FCSTD DOCUMENT  (FreeCAD 0.16R6712 (Git))
Label: 20180220234525!LT_master_cad
License: All rights reserved
LicenseURL: http://en.wikipedia.org/wiki/All_rights_reserved
objects: Part::Feature×46, App::FeaturePython×30, Part::FeaturePython×23, App::DocumentObjectGroup×11, Sketcher::SketchObject×10, Part::Box×9, PartDesign::Pad×6, Part::Cylinder×5, Part::Compound×4, Part::MultiFuse×4, PartDesign::Pocket×2, Part::Cut×1, Part::Mirroring×1
note: 119 computed .brp shape members not serialized (recipe doc carries the construction recipe); baked Part::Feature solids carry a one-line shape summary decoded from their .brp

FEATURE [Part::Feature] Clone007  label="Cab - bottom right"
  Placement = pos=(-85.7284,2481.18,-691.277) rot=(0.57735,-0.57735,0.57735;4.18879rad)
  shape: bbox 1016 x 101.6 x 101.6 mm, 46 faces (baked)
FEATURE [Part::Feature] Clone012  label="Cab - bottom left"
  Placement = pos=(-84.0606,1566.05,-690.228) rot=(0.57735,-0.57735,0.57735;4.18879rad)
  shape: bbox 1016 x 101.6 x 101.6 mm, 46 faces (baked)
FEATURE [Part::Feature] Clone021  label="Cab - bottom rear"
  Placement = pos=(-34.9284,1617.58,-691.277) rot=(-1,0,0;1.5708rad)
  shape: bbox 101.6 x 812.8 x 101.6 mm, 38 faces (baked)
FEATURE [Part::Feature] Clone022  label="Cab - bottom front"
  Placement = pos=(879.472,1620.02,-691.277) rot=(-1,0,0;1.5708rad)
  shape: bbox 101.6 x 812.8 x 101.6 mm, 38 faces (baked)
FEATURE [Part::Box] Box002  label="Cab Vert 1"
  Height = 1422.4
  Length = 101.6
  Placement = pos=(830.339,1515.25,-639.428) rot=(0,0,1;0rad)
  Width = 101.6
FEATURE [Part::Feature] Box003  label="Cab Vert 2"
  Placement = pos=(-84.0606,1515.25,-639.428) rot=(0,0,1;0rad)
  shape: bbox 101.6 x 101.6 x 1321 mm, 6 faces (baked)
FEATURE [Part::Feature] Box004  label="Cab Vert 3"
  Placement = pos=(828.672,2430.38,-640.477) rot=(0,0,1;0rad)
  shape: bbox 101.6 x 101.6 x 1321 mm, 6 faces (baked)
FEATURE [Part::Feature] Box005  label="Cab Vert 4"
  Placement = pos=(-86.1858,2430.38,-640.477) rot=(0,0,1;0rad)
  shape: bbox 101.6 x 101.6 x 1321 mm, 6 faces (baked)
FEATURE [Part::Feature] Clone023  label="Cab - bottom right001"
  Placement = pos=(-92.3505,2481.18,731.123) rot=(0.57735,-0.57735,0.57735;4.18879rad)
  shape: bbox 1016 x 101.6 x 101.6 mm, 46 faces (baked)
FEATURE [Part::Feature] Clone024  label="Cab - bottom front001"
  Placement = pos=(872.85,1620.02,731.123) rot=(-1,0,0;1.5708rad)
  shape: bbox 101.6 x 812.8 x 101.6 mm, 38 faces (baked)
FEATURE [Part::Feature] Clone025  label="Cab - bottom left001"
  Placement = pos=(-90.6827,1566.05,732.172) rot=(0.57735,-0.57735,0.57735;4.18879rad)
  shape: bbox 1016 x 101.6 x 101.6 mm, 46 faces (baked)
FEATURE [Part::Feature] Clone026  label="Cab - bottom rear001"
  Placement = pos=(-41.5505,1617.58,731.123) rot=(-1,0,0;1.5708rad)
  shape: bbox 101.6 x 812.8 x 101.6 mm, 38 faces (baked)
FEATURE [Part::Cylinder] Cylinder014  label="Person"
  Angle = 360
  Height = 1524
  Placement = pos=(-1660.29,1661.1,-1132.53) rot=(0,0,1;0rad)
  Radius = 254
FEATURE [Part::Box] Box006  label="Cab Top"
  Height = 3.175
  Length = 1016
  Placement = pos=(-92.3505,1516.16,787.4) rot=(0,0,1;0rad)
  Width = 1016
FEATURE [Part::Box] Box007  label="Cab Side"
  Height = 1524
  Length = 1016
  Placement = pos=(-84.8788,1511.3,-739.16) rot=(0,0,1;0rad)
  Width = 3.175
FEATURE [Part::Feature] Box008  label="Cab Side001"
  Placement = pos=(-93.1687,2532.38,-739.16) rot=(0,0,1;0rad)
  shape: bbox 1016 x 3.175 x 1524 mm, 6 faces (baked)
FEATURE [Part::Feature] Box009  label="Cab Side002"
  Placement = pos=(-93.98,2529.04,-739.16) rot=(0,0,-1;1.5708rad)
  shape: bbox 3.175 x 1016 x 1524 mm, 6 faces (baked)
FEATURE [Part::Feature] Box010  label="Cab Side003"
  Placement = pos=(-88.1961,2529.04,-739.16) rot=(0,0,-1;1.5708rad)
  shape: bbox 3.175 x 1016 x 1524 mm, 6 faces (baked)
FEATURE [Part::Box] Box011  label="Cab Bottom"
  Height = 3.175
  Length = 1016
  Placement = pos=(-92.3505,1516.16,-746.76) rot=(0,0,1;0rad)
  Width = 1016
FEATURE [App::DocumentObjectGroup] Group  label="Cab"
  Group = -> [Box005,Box004,Box003,Box002,Clone007,Clone012,Clone021,Clone022,Box006,Box007,Box008,Box009,Box010,Box011,Clone023,Clone024,Clone025,Clone026]
FEATURE [Part::Feature] Clone034  label="Frame - horizontal R"
  Placement = pos=(-1253.88,1464.81,-791.981) rot=(0,1,0;1.5708rad)
  shape: bbox 2134 x 101.6 x 101.6 mm, 90 faces (baked)
FEATURE [Part::Feature] Box  label="PowerCube005"
  Placement = pos=(-1231.18,2023.04,-741.072) rot=(0,0,1;0rad)
  shape: bbox 762 x 508 x 508 mm, 6 faces (baked)
FEATURE [Part::Feature] Box014  label="PowerCube006"
  Placement = pos=(-1228.85,1515.61,-739.279) rot=(0,0,1;0rad)
  shape: bbox 762 x 508 x 508 mm, 6 faces (baked)
FEATURE [Part::Feature] Compound022  label="Idler007"
  Placement = pos=(464.548,1400.81,-1066.8) rot=(0,0,1;0rad)
  shape: bbox 302.3 x 217 x 302.3 mm, 148 faces, 13 solids (baked)
FEATURE [Part::Feature] Compound  label="Idler008"
  Placement = pos=(-948.365,1400.81,-1066.8) rot=(0,0,1;0rad)
  shape: bbox 302.3 x 217 x 302.3 mm, 148 faces, 13 solids (baked)
FEATURE [Part::Feature] Compound025  label="Idler011"
  Placement = pos=(464.566,2966.33,-1066.8) rot=(0,0,1;0rad)
  shape: bbox 302.3 x 217 x 302.3 mm, 148 faces, 13 solids (baked)
FEATURE [Part::FeaturePython] PathArray002  # WARN: FeaturePython — macro-defined, semantics opaque (R4)
  Align = true
  Count = 52
  Placement = pos=(0,1235.71,0) rot=(0,0,1;0rad)
  Xlate = (0,0,0)
FEATURE [Part::FeaturePython] PathArray003  # WARN: FeaturePython — macro-defined, semantics opaque (R4)
  Align = true
  Count = 52
  Placement = pos=(0,2810.51,0) rot=(0,0,1;0rad)
  Xlate = (0,0,0)
FEATURE [Part::Cylinder] Cylinder
  Angle = 360
  Height = 1828.8
  Placement = pos=(-892.81,1108.71,-914.4) rot=(0.57735,-0.57735,-0.57735;4.18879rad)
  Radius = 38.1
FEATURE [Part::Cylinder] Cylinder018
  Angle = 360
  Height = 1828.8
  Placement = pos=(520.7,1108.71,-914.4) rot=(0.57735,-0.57735,-0.57735;4.18879rad)
  Radius = 38.1
FEATURE [Part::Feature] Compound026  label="Idler012"
  Placement = pos=(-947.42,2966.33,-1066.8) rot=(0,0,1;0rad)
  shape: bbox 302.3 x 217 x 302.3 mm, 148 faces, 13 solids (baked)
FEATURE [Part::Feature] Cylinder035
  Placement = pos=(1556.05,1344.57,-44.0571) rot=(-0.577258,0.577258,-0.577534;2.09412rad)
  shape: bbox 812.8 x 76.2 x 76.59 mm, 3 faces (baked)
FEATURE [Part::Feature] Cylinder036
  Placement = pos=(2058.87,1344.57,-43.8629) rot=(-0.577258,0.577258,-0.577534;2.09412rad)
  shape: bbox 508 x 35.56 x 35.8 mm, 3 faces (baked)
FEATURE [Part::Feature] Cylinder037
  Placement = pos=(2551.89,1307.89,-43.6273) rot=(-1,-0.000239,-0.000239;1.5708rad)
  shape: bbox 50.8 x 76.2 x 50.8 mm, 3 faces (baked)
FEATURE [Part::Feature] Cylinder038
  Placement = pos=(1377.14,1307.13,-44.0667) rot=(-1,-0.000239,-0.000239;1.5708rad)
  shape: bbox 50.8 x 76.2 x 50.8 mm, 3 faces (baked)
FEATURE [Part::Feature] Compound031  label="Idler013"
  Placement = pos=(-210.82,2966.21,-1066.8) rot=(0,0,1;0rad)
  shape: bbox 302.3 x 217 x 302.3 mm, 148 faces, 13 solids (baked)
FEATURE [Part::Feature] Compound033  label="Idler015"
  Placement = pos=(-210.82,1391.41,-1066.8) rot=(0,0,1;0rad)
  shape: bbox 302.3 x 217 x 302.3 mm, 148 faces, 13 solids (baked)
FEATURE [Part::Cylinder] Cylinder043
  Angle = 360
  Height = 1828.8
  Placement = pos=(-156.21,1108.71,-914.4) rot=(0.57735,-0.57735,-0.57735;4.18879rad)
  Radius = 38.1
FEATURE [App::DocumentObjectGroup] Group004  label="Idlers"
  Group = -> [Cylinder018,Cylinder,Compound026,Compound025,Compound,Compound022,Cylinder043,Compound031,Compound033]
FEATURE [Part::Feature] Box015  label="PowerCube007"
  Placement = pos=(-1180.34,2023.04,-233.172) rot=(0,0,1;0rad)
  shape: bbox 762 x 508 x 508 mm, 6 faces (baked)
FEATURE [Part::Feature] Box016  label="PowerCube008"
  Placement = pos=(-1180.34,1515.11,-233.172) rot=(0,0,1;0rad)
  shape: bbox 762 x 508 x 508 mm, 6 faces (baked)
FEATURE [Part::Box] Box017  label="Cube"
  Height = 1524
  Length = 1041.4
  Placement = pos=(-266.7,1567.18,-736.6) rot=(0,0,1;0rad)
  Width = 914.4
FEATURE [Part::Feature] Clone063001  label="LT_arm_shaft"
  Placement = pos=(-1028.09,1261.61,54.5351) rot=(0.57735,-0.57735,-0.57735;4.18879rad)
  shape: bbox 76.2 x 1524 x 76.2 mm, 3 faces (baked)
FEATURE [Sketcher::SketchObject] Sketch
  ExternalGeometry = -> [Cylinder035]
  Placement = pos=(1556.05,1344.57,-44.0571) rot=(-0.577442,0.577442,0.577166;4.18851rad)
  Support = -> Cylinder035 [Face3]
  sketch-geometry (1):
    g0: Circle CenterX=5e-12 CenterY=0 CenterZ=0 NormalX=0 NormalY=0 NormalZ=1 Radius=38.1
  constraints (2):
    c: Coincident(g0,g-3)
    c: Tangent(g0,g-3)
FEATURE [PartDesign::Pad] Pad008
  Length = 152.4
  Length2 = 100
  Placement = pos=(1556.05,1344.57,-44.0571) rot=(-0.577258,0.577258,-0.577534;2.09412rad)
  Sketch = -> Sketch
  Type = 0
FEATURE [Part::Feature] Cylinder044
  Placement = pos=(3466.29,1307.89,-196.027) rot=(-1,-0.000239,-0.000239;1.5708rad)
  shape: bbox 50.8 x 76.2 x 50.8 mm, 3 faces (baked)
FEATURE [Part::Feature] Cylinder045
  Placement = pos=(2724.36,1344.57,-196.263) rot=(-0.577258,0.577258,-0.577534;2.09412rad)
  shape: bbox 508 x 35.56 x 35.8 mm, 3 faces (baked)
FEATURE [Part::Feature] Cylinder046
  Placement = pos=(1377.14,1307.13,-196.467) rot=(-1,-0.000239,-0.000239;1.5708rad)
  shape: bbox 50.8 x 76.2 x 50.8 mm, 3 faces (baked)
FEATURE [Sketcher::SketchObject] Sketch016
  ExternalGeometry = -> [Cylinder045]
  Placement = pos=(2724.36,1344.57,-196.263) rot=(-0.577442,0.577442,0.577166;4.18851rad)
  Support = -> Cylinder045 [Face3]
  sketch-geometry (1):
    g0: Circle CenterX=0 CenterY=0 CenterZ=0 NormalX=0 NormalY=0 NormalZ=1 Radius=17.78
  constraints (2):
    c: Coincident(g0,g-1)
    c: Tangent(g0,g-3)
FEATURE [PartDesign::Pad] Pad008003
  Length = 609.6
  Length2 = 100
  Placement = pos=(2724.36,1344.57,-196.263) rot=(-0.577258,0.577258,-0.577534;2.09412rad)
  Sketch = -> Sketch016
  Type = 0
FEATURE [Part::FeaturePython] Arm_support_01  # a2plus imported part (geometry in sourceFile) (typed FeaturePython)
  Placement = pos=(-359.342,1668.01,-741.182) rot=(0,0,1;0rad)
  fixedPosition = true
  sourceFile = <userpath>/Documents/Freecad docs/Tractor/LT/Arm support.fcstd
  timeLastImport = 1.50929e+09
  updateColors = true
FEATURE [Part::Feature] Arm_support_01003  label="Arm_support_004"
  Placement = pos=(-359.342,2379.21,-741.182) rot=(0,0,1;0rad)
  shape: bbox 101.6 x 101.6 x 1016 mm, 46 faces (baked)
FEATURE [Part::Feature] Arm_support_01004  label="10 hole tubing front"
  Placement = pos=(727.318,2531.61,-791.982) rot=(1,0,0;1.5708rad)
  shape: bbox 101.6 x 1016 x 101.6 mm, 46 faces (baked)
FEATURE [App::FeaturePython] planeConstraint01  label="10 hole tubing front 1"  # a2plus constraint (typed FeaturePython)
  Object1 = Arm_support_01004
  Object2 = Arm_support_01
  SubElement1 = Face4
  SubElement2 = Face1
  Type = plane
  directionConstraint = 1
  offset = 203.2
FEATURE [App::FeaturePython] planeConstraint01_mirror  label="planeConstraint01__Arm_support_005"  # a2plus constraint (typed FeaturePython)
  Object1 = Arm_support_01004
  Object2 = Arm_support_01
  SubElement1 = Face4
  SubElement2 = Face1
  Type = plane
  directionConstraint = 1
  offset = 203.2
FEATURE [App::FeaturePython] planeConstraint02  label="10 hole tubing front 2"  # a2plus constraint (typed FeaturePython)
  Object1 = Arm_support_01004
  Object2 = Arm_support_01
  SubElement1 = Face1
  SubElement2 = Face3
  Type = plane
  directionConstraint = 0
  offset = 0
FEATURE [App::FeaturePython] planeConstraint02_mirror  label="planeConstraint02__Arm_support_005"  # a2plus constraint (typed FeaturePython)
  Object1 = Arm_support_01004
  Object2 = Arm_support_01
  SubElement1 = Face1
  SubElement2 = Face3
  Type = plane
  directionConstraint = 0
  offset = 0
FEATURE [App::FeaturePython] planeConstraint03  label="planeConstraint03__Arm_support_005"  # a2plus constraint (typed FeaturePython)
  Object1 = Arm_support_01
  Object2 = Arm_support_01004
  SubElement1 = Face5
  SubElement2 = Face5
  Type = plane
  directionConstraint = 0
  offset = -1086.66
FEATURE [App::FeaturePython] planeConstraint03_mirror  label="10 hole tubing front 3"  # a2plus constraint (typed FeaturePython)
  Object1 = Arm_support_01
  Object2 = Arm_support_01004
  SubElement1 = Face5
  SubElement2 = Face5
  Type = plane
  directionConstraint = 0
  offset = -1086.66
FEATURE [Part::Feature] Arm_support_01005  label="10 hole tubing rear"
  Placement = pos=(-1203.08,2531.61,-791.982) rot=(1,0,0;1.5708rad)
  shape: bbox 101.6 x 1016 x 101.6 mm, 46 faces (baked)
FEATURE [Part::Feature] Arm_support_01006  label="10 hole tubing mid 1"
  Placement = pos=(-720.479,2531.61,-791.982) rot=(1,0,0;1.5708rad)
  shape: bbox 101.6 x 1016 x 101.6 mm, 46 faces (baked)
FEATURE [Part::Feature] Pad008003002  label="Pad008005"
  Placement = pos=(-1.27,0,0) rot=(0,0,1;0rad)
  shape: bbox 965.2 x 76.2 x 76.66 mm, 3 faces (baked)
FEATURE [Part::Feature] Pad008003003  label="Pad008006"
  Placement = pos=(-1.27,0,-152.4) rot=(0,0,1;0rad)
  shape: bbox 965.2 x 76.2 x 76.66 mm, 3 faces (baked)
FEATURE [Part::Feature] Pad008003004  label="Pad008007"
  Placement = pos=(242.56,0,0) rot=(0,0,1;0rad)
  shape: bbox 1118 x 35.56 x 36.09 mm, 3 faces (baked)
FEATURE [Part::Compound] Compound001004
  Links = -> [Pad008003002,Cylinder036,Cylinder037,Cylinder038]
FEATURE [Part::Compound] Compound001005
  Links = -> [Pad008003004,Cylinder046,Cylinder044,Pad008003003]
FEATURE [App::DocumentObjectGroup] Group009  label="Cylinders (edit here)"
  Group = -> [Cylinder035,Pad008,Cylinder045,Pad008003,Compound001004,Compound001005]
FEATURE [Part::Box] Box020  label="Cube001"
  Height = 508
  Length = 508
  Placement = pos=(-943.542,1515.61,-741.182) rot=(0,0,1;0rad)
  Width = 330.2
FEATURE [Part::Box] Box021  label="Cube002"
  Height = 508
  Length = 508
  Placement = pos=(-943.542,2201.41,-741.182) rot=(0,0,1;0rad)
  Width = 330.2
FEATURE [Part::Box] Box022  label="Cube003"
  Height = 508
  Length = 508
  Placement = pos=(-943.542,1769.61,-741.182) rot=(0,0,1;1.5708rad)
  Width = 330.2
FEATURE [Part::Box] Box023  label="Cube004"
  Height = 508
  Length = 508
  Placement = pos=(-918.14,1642.61,-233.182) rot=(0,0,1;0rad)
  Width = 762
FEATURE [App::DocumentObjectGroup] Group013  label="Small PC"
  Group = -> [Box020,Box021,Box022,Box023]
FEATURE [App::DocumentObjectGroup] Group002  label="Power Cube"
  Group = -> [Box,Box014,Box015,Box016,Group013]
FEATURE [Part::Feature] Arm_support_01006001  label="10 hole tubing mid 2"
  Placement = pos=(-359.342,2531.61,-791.982) rot=(1,0,0;1.5708rad)
  shape: bbox 101.6 x 1016 x 101.6 mm, 46 faces (baked)
FEATURE [App::FeaturePython] planeConstraint26  label="10 hole mid 2"  # a2plus constraint (typed FeaturePython)
  Object1 = Arm_support_01006001
  Object2 = Arm_support_01
  SubElement1 = Face5
  SubElement2 = Face5
  Type = plane
  directionConstraint = 0
  offset = 0
FEATURE [App::FeaturePython] planeConstraint26_mirror  label="planeConstraint26__10 hole tubing mid 2"  # a2plus constraint (typed FeaturePython)
  Object1 = Arm_support_01006001
  Object2 = Arm_support_01
  SubElement1 = Face5
  SubElement2 = Face5
  Type = plane
  directionConstraint = 0
  offset = 0
FEATURE [App::FeaturePython] planeConstraint27_mirror001  label="planeConstraint27__Arm_support_004"  # a2plus constraint (typed FeaturePython)
  Object1 = Arm_support_01003
  Object2 = Arm_support_01
  SubElement1 = Face16
  SubElement2 = Face16
  Type = plane
  directionConstraint = 0
  offset = -711.2
FEATURE [Part::Feature] Compound001001  label="Track tensioner"
  Placement = pos=(105.497,-20.1003,38.1) rot=(0,0,1;0rad)
  shape: bbox 248.4 x 1599 x 248.4 mm, 472 faces, 10 solids (baked)
FEATURE [App::DocumentObjectGroup] Group005  label="Tracks"
  Group = -> [PathArray002,PathArray003,Compound001001]
FEATURE [App::FeaturePython] planeConstraint28  label="tensioner 1"  # a2plus constraint (typed FeaturePython)
  Object1 = Compound001001
  Object2 = Arm_support_01
  SubElement1 = Face52
  SubElement2 = Face1
  Type = plane
  directionConstraint = 1
  offset = -1.27
FEATURE [App::FeaturePython] planeConstraint28_mirror  label="planeConstraint28__Compound002"  # a2plus constraint (typed FeaturePython)
  Object1 = Compound001001
  Object2 = Arm_support_01
  SubElement1 = Face52
  SubElement2 = Face1
  Type = plane
  directionConstraint = 1
  offset = -1.27
FEATURE [App::FeaturePython] planeConstraint29  label="planeConstraint29__Compound002"  # a2plus constraint (typed FeaturePython)
  Object1 = Arm_support_01
  Object2 = Compound001001
  SubElement1 = Face5
  SubElement2 = Face51
  Type = plane
  directionConstraint = 1
  offset = -1.27
FEATURE [App::FeaturePython] planeConstraint29_mirror  label="tensioner 2"  # a2plus constraint (typed FeaturePython)
  Object1 = Arm_support_01
  Object2 = Compound001001
  SubElement1 = Face5
  SubElement2 = Face51
  Type = plane
  directionConstraint = 1
  offset = -1.27
FEATURE [App::DocumentObjectGroup] Group011  label="Constraints (permanent)"
  Group = -> [Arm_support_01,planeConstraint01,planeConstraint02,planeConstraint03_mirror,planeConstraint26,planeConstraint28,planeConstraint29_mirror]
FEATURE [Part::FeaturePython] Clone063026  label="8 hole tubing"  # WARN: FeaturePython — macro-defined, semantics opaque (R4)
  Placement = pos=(-1213.84,1566.41,-754.372) rot=(0,1,0;0.202167rad)
  Scale = (1,1,1)
FEATURE [Part::FeaturePython] Clone063027  label="8 hole tubing001"  # WARN: FeaturePython — macro-defined, semantics opaque (R4)
  Placement = pos=(-1106.73,2480.81,22.8013) rot=(0,1,0;1.32645rad)
  Scale = (1,1,1)
FEATURE [Part::FeaturePython] Clone063028  label="8 hole tubing002"  # WARN: FeaturePython — macro-defined, semantics opaque (R4)
  Placement = pos=(-1213.84,2480.81,-754.372) rot=(0,1,0;0.202167rad)
  Scale = (1,1,1)
FEATURE [Part::FeaturePython] Clone063029  label="8 hole tubing003"  # WARN: FeaturePython — macro-defined, semantics opaque (R4)
  Placement = pos=(-1106.73,1566.41,22.8013) rot=(0,1,0;1.32645rad)
  Scale = (1,1,1)
FEATURE [Part::FeaturePython] Clone063033  label="Cylinder 36in retracted"  # Draft clone (typed FeaturePython)
  Objects = -> [Compound001004]
  Placement = pos=(-1736.48,119.579,-239.915) rot=(0,0,1;0rad)
  Scale = (1,1,1)
FEATURE [Part::FeaturePython] Clone063034  label="Cylinder 36in extended"  # Draft clone (typed FeaturePython)
  Objects = -> [Compound001005]
  Placement = pos=(-557.972,119.579,-1660.81) rot=(0,-1,0;1.56923rad)
  Scale = (1,1,1)
FEATURE [Sketcher::SketchObject] Sketch024  label="Arm-Cylinder geometry"
  Placement = pos=(-15.2649,852.156,-47.0649) rot=(1,0,0;1.5708rad)
  sketch-geometry (38):
    g0: LineSegment StartX=1203.73 StartY=-906.649 StartZ=0 EndX=1301 EndY=-728.242 EndZ=0
    g1: LineSegment StartX=1301 StartY=-728.242 StartZ=0 EndX=2088.08 EndY=-1092.2 EndZ=0
    g2: LineSegment StartX=601.383 StartY=-1092.2 StartZ=0 EndX=1685.52 EndY=-1092.2 EndZ=0
    g3: LineSegment StartX=-1012.82 StartY=101.6 StartZ=0 EndX=1203.73 EndY=-906.649 EndZ=0
    g4: Circle [constr] CenterX=-1012.82 CenterY=101.6 CenterZ=0 NormalX=0 NormalY=0 NormalZ=1 Radius=2435.1
    g5: LineSegment StartX=565.984 StartY=2188.85 StartZ=0 EndX=1016.32 EndY=1447.8 EndZ=0
    g6: LineSegment StartX=385.75 StartY=2095.01 StartZ=0 EndX=565.984 EndY=2188.85 EndZ=0
    g7: LineSegment StartX=-1012.82 StartY=101.6 StartZ=0 EndX=385.75 EndY=2095.01 EndZ=0
    g8: LineSegment StartX=-252.055 StartY=-693.674 StartZ=0 EndX=789.345 EndY=-693.674 EndZ=0
    g9: LineSegment StartX=789.345 StartY=-693.674 StartZ=0 EndX=789.345 EndY=830.326 EndZ=0
    g10: LineSegment StartX=789.345 StartY=830.326 StartZ=0 EndX=-252.055 EndY=830.326 EndZ=0
    g11: LineSegment StartX=-252.055 StartY=830.326 StartZ=0 EndX=-252.055 EndY=-693.674 EndZ=0
    g12: LineSegment StartX=-1012.82 StartY=101.6 StartZ=0 EndX=904.459 EndY=-143.324 EndZ=0
    g13: LineSegment StartX=904.459 StartY=-143.324 StartZ=0 EndX=1203.73 EndY=-906.649 EndZ=0
    g14: LineSegment StartX=-1012.82 StartY=101.6 StartZ=0 EndX=-419.585 EndY=1941.17 EndZ=0
    g15: LineSegment StartX=-419.585 StartY=1941.17 StartZ=0 EndX=385.75 EndY=2095.01 EndZ=0
    g16: LineSegment StartX=-395.479 StartY=2049.21 StartZ=0 EndX=-276.62 EndY=1968.48 EndZ=0
    g17: LineSegment StartX=-342.9 StartY=-236.474 StartZ=0 EndX=831.85 EndY=-236.474 EndZ=0
    g18: LineSegment StartX=-341.372 StartY=1852.68 StartZ=0 EndX=-342.9 EndY=-236.474 EndZ=0
    g19: LineSegment StartX=-1012.82 StartY=101.6 StartZ=0 EndX=-341.372 EndY=1852.68 EndZ=0
    g20: LineSegment StartX=-1012.82 StartY=101.6 StartZ=0 EndX=831.85 EndY=-236.474 EndZ=0
    g21: LineSegment StartX=1015.09 StartY=-147.156 StartZ=0 EndX=957.587 EndY=-278.831 EndZ=0
    g22: LineSegment StartX=1015.09 StartY=-147.156 StartZ=0 EndX=1203.73 EndY=-906.649 EndZ=0
    g23: LineSegment StartX=-395.479 StartY=2049.21 StartZ=0 EndX=385.75 EndY=2095.01 EndZ=0
    g24: LineSegment StartX=1015.09 StartY=-147.156 StartZ=0 EndX=883.415 EndY=-89.6516 EndZ=0
    g25: LineSegment StartX=-395.479 StartY=2049.21 StartZ=0 EndX=-476.211 EndY=1930.35 EndZ=0
    g26: LineSegment StartX=-395.479 StartY=2049.21 StartZ=0 EndX=214.076 EndY=2137.74 EndZ=0
    g27: LineSegment StartX=214.076 StartY=2137.74 StartZ=0 EndX=565.984 EndY=2188.85 EndZ=0
    g28: LineSegment StartX=1301 StartY=-728.242 StartZ=0 EndX=1029.07 EndY=-175.57 EndZ=0
    g29: LineSegment StartX=1015.09 StartY=-147.156 StartZ=0 EndX=1029.07 EndY=-175.57 EndZ=0
    g30: LineSegment StartX=963.525 StartY=-293.978 StartZ=0 EndX=831.85 EndY=-236.474 EndZ=0
    g31: LineSegment StartX=831.85 StartY=-236.474 StartZ=0 EndX=889.354 EndY=-104.799 EndZ=0
    g32: LineSegment StartX=-260.64 StartY=1971.53 StartZ=0 EndX=-341.372 EndY=1852.68 EndZ=0
    g33: LineSegment StartX=-341.372 StartY=1852.68 StartZ=0 EndX=-460.231 EndY=1933.41 EndZ=0
    g34: LineSegment StartX=1203.73 StartY=-906.649 StartZ=0 EndX=1353.99 EndY=-1092.2 EndZ=0
    g35: LineSegment StartX=1353.99 StartY=-1092.2 StartZ=0 EndX=2088.08 EndY=-1092.2 EndZ=0
    g36: LineSegment StartX=406.99 StartY=1857.2 StartZ=0 EndX=1016.32 EndY=1447.8 EndZ=0
    g37: LineSegment StartX=385.75 StartY=2095.01 StartZ=0 EndX=406.99 EndY=1857.2 EndZ=0
  constraints (106):
    c: Coincident(g1,g0)
    c: Horizontal(g2)
    c: Coincident(g3,g0)
    c: DistanceX(g8) = -252.055
    c: Distance(g0) = 203.2
    c: Distance(g1) = 867.156
    c: PointOnObject(g0,g4)
    c: Coincident(g5,g6)
    c: Coincident(g7,g6)
    c: Equal(g3,g7) = 2071.24
    c: Equal(g0,g6) = 238.711
    c: Equal(g1,g5) = 1020.15
    c: Coincident(g8,g9)
    c: Coincident(g9,g10)
    c: Coincident(g10,g11)
    c: Coincident(g11,g8)
    c: Horizontal(g8)
    c: Horizontal(g10)
    c: Vertical(g9)
    c: Vertical(g11)
    c: Distance(g10) = 1041.4
    c: Distance(g9) = 1524
    c: Coincident(g12,g13)
    c: Coincident(g13,g0)
    c: Coincident(g14,g15)
    c: Equal(g12,g14) = 1727.2
    c: Equal(g13,g15) = 711.2
    c: DistanceY(g2) = -1092.2
    c: Distance(g5,g2) = 2540
    c: Distance(g18,g14) = 101.6
    c: PointOnObject(g16,g15)
    c: Distance(g16,g15) = 101.6
    c: Distance(g17) = 1174.75
    c: Coincident(g18,g17)
    c: Distance(g18) = 2089.15
    c: Equal(g19,g20)
    c: PointOnObject(g21,g13)
    c: Distance(g21,g13) = 101.6
    c: Coincident(g22,g0)
    c: Equal(g23,g22)
    c: DistanceY(g8) = -693.674
    c: Distance(g17,g8) = 457.2
    c: PointOnObject(g5,g4)
    c: Horizontal(g17)
    c: Coincident(g23,g16)
    c: Coincident(g22,g21)
    c: Coincident(g24,g21)
    c: PointOnObject(g24,g13)
    c: Perpendicular(g21,g24)
    c: Equal(g24,g21)
    c: Coincident(g25,g16)
    c: Equal(g25,g16)
    c: Perpendicular(g16,g25)
    c: PointOnObject(g25,g15)
    c: Coincident(g27,g5)
    c: Coincident(g26,g27)
    c: Coincident(g26,g16)
    c: Parallel(g27,g26)
    c: Distance(g27) = 355.6
    c: Coincident(g28,g0)
    c: Equal(g26,g28)
    c: Distance(g26) = 615.95
    c: Coincident(g29,g21)
    c: Coincident(g29,g28)
    c: Parallel(g29,g28)
    c: Coincident(g17,g20)
    c: Coincident(g17,g30)
    c: Coincident(g17,g31)
    c: Perpendicular(g30,g31)
    c: Equal(g31,g30)
    c: PointOnObject(g30,g13)
    c: PointOnObject(g31,g13)
    c: Distance(g17,g13) = 101.6
    c: Perpendicular(g32,g33)
    c: Equal(g33,g32)
    c: PointOnObject(g33,g15)
    c: Coincident(g32,g33)
    c: PointOnObject(g32,g15)
    c: Coincident(g32,g18)
    c: Coincident(g32,g19)
    c: Distance(g18,g15) = 101.6
    c: Coincident(g3,g4)
    c: Coincident(g3,g7)
    c: Coincident(g3,g12)
    c: Coincident(g3,g14)
    c: Coincident(g3,g19)
    c: Coincident(g3,g20)
    c: DistanceX(g17) = -342.9
    c: Coincident(g0,g34)
    c: Coincident(g34,g35)
    c: Coincident(g35,g1)
    c: Distance(g34) = 238.76
    c: Angle(g35,g34) = 2.25147
    c: Angle(g34,g0) = 1.96175
    c: Coincident(g37,g36)
    c: Equal(g34,g37) = 238.76
    c: Angle(g36,g37) = 2.25147
    c: Coincident(g15,g23)
    c: Coincident(g15,g6)
    c: Coincident(g6,g37)
    c: Coincident(g36,g5)
    c: Angle(g37,g6) = 1.96175
    c: DistanceY(g24) = -89.6516
    c: Horizontal(g35)
    c: PointOnObject(g1,g2)
    c: DistanceY(g-1,g3) = 101.6
FEATURE [Part::Cylinder] Cylinder047  label="Loader cylinder shaft"
  Angle = 360
  Height = 1219.2
  Placement = pos=(-359.342,1414.01,-283.982) rot=(-1,0,0;1.5708rad)
  Radius = 25.4
FEATURE [App::FeaturePython] planeConstraint30_mirror  label="planeConstraint30__Arm_support_01"  # a2plus constraint (typed FeaturePython)
  Object1 = Arm_support_01
  Object2 = Pocket002
  SubElement1 = Face16
  SubElement2 = Face1
  Type = plane
  directionConstraint = 1
  offset = 0
FEATURE [App::FeaturePython] axialConstraint04_mirror  label="axialConstraint04__Arm_support_01"  # a2plus constraint (typed FeaturePython)
  Object1 = Arm_support_01
  Object2 = Pocket002
  SubElement1 = Edge30
  SubElement2 = Edge15
  Type = axial
  directionConstraint = 1
  lockRotation = false
FEATURE [Part::Feature] Compound001  label="Lowered bucket"
  Placement = pos=(2340.99,3211.4,388.012) rot=(0,-1,0;0.240855rad)
  shape: bbox 1093 x 1829 x 510.4 mm, 626 faces, 28 solids (baked)
FEATURE [Part::Feature] Compound001009  label="Raised bucket"
  Placement = pos=(2138.11,3211.4,2098.75) rot=(0,1,0;0.5916rad)
  shape: bbox 788.7 x 1829 x 923.9 mm, 626 faces, 28 solids (baked)
FEATURE [Part::Feature] Fusion002002002  label="14" cylinder ret"
  Placement = pos=(-2279.03,188.997,-2348.22) rot=(0.62855,0.729863,-0.268748;1.8185rad)
  shape: bbox 298.4 x 50.8 x 614.8 mm, 38 faces (baked)
FEATURE [Part::Feature] Fusion002002001  label="14" cylinder ext"
  Placement = pos=(146.458,-4455.83,-1155.72) rot=(0.957629,0.161054,0.238764;1.1564rad)
  shape: bbox 1013 x 50.8 x 186 mm, 38 faces (baked)
FEATURE [App::FeaturePython] circularEdgeConstraint10  label="curl cylinder ret"  # a2plus constraint (typed FeaturePython)
  Object1 = Fusion002002002
  Object2 = Compound001
  SubElement1 = Edge79
  SubElement2 = Edge986
  Type = circularEdge
  directionConstraint = 1
  lockRotation = false
  offset = 0
FEATURE [App::FeaturePython] circularEdgeConstraint11  label="curl cylinder ext"  # a2plus constraint (typed FeaturePython)
  Object1 = Fusion002002001
  Object2 = Compound001009
  SubElement1 = Edge62
  SubElement2 = Edge986
  Type = circularEdge
  directionConstraint = 1
  lockRotation = false
  offset = 0
FEATURE [Sketcher::SketchObject] Sketch031
  Placement = pos=(879.717,1464.81,-791.981) rot=(0,1,0;1.5708rad)
  Support = -> Clone034 [Face4]
  sketch-geometry (4):
    g0: LineSegment StartX=-50.8 StartY=-50.8 StartZ=0 EndX=50.8 EndY=-50.8 EndZ=0
    g1: LineSegment StartX=50.8 StartY=-50.8 StartZ=0 EndX=50.8 EndY=50.8 EndZ=0
    g2: LineSegment StartX=50.8 StartY=50.8 StartZ=0 EndX=-50.8 EndY=50.8 EndZ=0
    g3: LineSegment StartX=-50.8 StartY=50.8 StartZ=0 EndX=-50.8 EndY=-50.8 EndZ=0
  constraints (8):
    c: Coincident(g0,g1)
    c: Coincident(g1,g2)
    c: Coincident(g2,g3)
    c: Coincident(g3,g0)
    c: Horizontal(g0)
    c: Horizontal(g2)
    c: Vertical(g1)
    c: Vertical(g3)
FEATURE [PartDesign::Pocket] Pocket
  Length = 101.6
  Placement = pos=(-1253.88,1464.81,-791.981) rot=(0,1,0;1.5708rad)
  Sketch = -> Sketch031
  Type = 0
FEATURE [Part::FeaturePython] Clone063040  label="Clone of Pocket"  # Draft clone (typed FeaturePython)
  Objects = -> [Pocket]
  Placement = pos=(-1253.88,2582.41,-791.981) rot=(0,1,0;1.5708rad)
  Scale = (1,1,1)
FEATURE [Part::FeaturePython] Clone063041  label="7 foot tubing002"  # WARN: FeaturePython — macro-defined, semantics opaque (R4)
  Placement = pos=(4633.48,2317.68,-87.4642) rot=(-0.550439,-0.550439,0.627721;2.02048rad)
  Scale = (1,1,1)
FEATURE [Sketcher::SketchObject] Sketch032  label="Arm-Cylinder geometry001"
  ExternalGeometry = -> [Clone063041]
  Placement = pos=(4633.48,2266.88,-87.4644) rot=(0.627722,-0.55044,0.550437;2.02048rad)
  Support = -> Clone063041 [Face2]
  sketch-geometry (6):
    g0: LineSegment StartX=0 StartY=2082.8 StartZ=0 EndX=0 EndY=149.939 EndZ=0
    g1: LineSegment StartX=0 StartY=149.939 StartZ=0 EndX=-719.25 EndY=-243.643 EndZ=0
    g2: LineSegment StartX=10.2177 StartY=39.7131 StartZ=0 EndX=-127.683 EndY=80.0693 EndZ=0
    g3: LineSegment StartX=10.2177 StartY=39.7131 StartZ=0 EndX=50.5739 EndY=177.613 EndZ=0
    g4: LineSegment StartX=-141.954 StartY=72.2597 StartZ=0 EndX=-101.598 EndY=210.158 EndZ=0
    g5: LineSegment StartX=-101.598 StartY=210.158 StartZ=0 EndX=36.3001 EndY=169.803 EndZ=0
  constraints (20):
    c: PointOnObject(g2,g1)
    c: Distance(g2,g1) = 101.6
    c: PointOnObject(g3,g1)
    c: Perpendicular(g2,g3)
    c: Equal(g3,g2)
    c: Perpendicular(g4,g5)
    c: Equal(g5,g4)
    c: PointOnObject(g4,g1)
    c: PointOnObject(g5,g1)
    c: Angle(g0,g1) = 2.0715
    c: Distance(g0) = 1932.86
    c: Distance(g1) = 819.894
    c: Distance(g5,g0) = 101.598
    c: Distance(g5,g1) = 101.599
    c: Distance(g2,g0) = 10.2177
    c: Coincident(g0,g1)
    c: Coincident(g4,g5)
    c: Coincident(g2,g3)
    c: Coincident(g-3,g0)
    c: PointOnObject(g0,g-2)
FEATURE [Sketcher::SketchObject] Sketch033
  Placement = pos=(4633.48,2317.68,-87.4642) rot=(0.60096,0.600957,0.52697;2.17161rad)
  Support = -> Clone063041 [Face3]
  sketch-geometry (5):
    g0: LineSegment StartX=50.8 StartY=-50.8 StartZ=0 EndX=50.8 EndY=50.8 EndZ=0
    g1: LineSegment StartX=50.8 StartY=50.8 StartZ=0 EndX=-50.8 EndY=50.8 EndZ=0
    g2: LineSegment StartX=-50.8 StartY=50.8 StartZ=0 EndX=-50.8 EndY=-50.8 EndZ=0
    g3: LineSegment StartX=-50.8 StartY=-50.8 StartZ=0 EndX=50.8 EndY=-50.8 EndZ=0
    g4: Circle [constr] CenterX=0 CenterY=0 CenterZ=0 NormalX=0 NormalY=0 NormalZ=1 Radius=71.842
  constraints (14):
    c: Coincident(g0,g1)
    c: Coincident(g1,g2)
    c: Coincident(g2,g3)
    c: Coincident(g3,g0)
    c: Equal(g0,g1)
    c: Equal(g0,g2)
    c: Equal(g0,g3)
    c: PointOnObject(g0,g4)
    c: PointOnObject(g1,g4)
    c: PointOnObject(g2,g4)
    c: PointOnObject(g3,g4)
    c: Coincident(g4,g-1)
    c: Horizontal(g3)
    c: Distance(g3) = 101.6
FEATURE [PartDesign::Pocket] Pocket003
  Length = 101.6
  Placement = pos=(4633.48,2317.68,-87.4642) rot=(-0.550439,-0.550439,0.627721;2.02048rad)
  Sketch = -> Sketch033
  Type = 0
FEATURE [Part::FeaturePython] Clone063042  label="7 hole tubing"  # WARN: FeaturePython — macro-defined, semantics opaque (R4)
  Placement = pos=(4686.58,2317.68,-721.479) rot=(0,-1,0;0.279253rad)
  Scale = (1,1,1)
FEATURE [App::FeaturePython] planeConstraint04  label="Arm 1"  # a2plus constraint (typed FeaturePython)
  Object1 = Clone063041
  Object2 = Pocket003
  SubElement1 = Face4
  SubElement2 = Face4
  Type = plane
  directionConstraint = 0
  offset = 0
FEATURE [App::FeaturePython] planeConstraint05  label="Arm 2"  # a2plus constraint (typed FeaturePython)
  Object1 = Clone063041
  Object2 = Pocket003
  SubElement1 = Face2
  SubElement2 = Face5
  Type = plane
  directionConstraint = 0
  offset = 0
FEATURE [App::FeaturePython] planeConstraint06  label="Arm 3"  # a2plus constraint (typed FeaturePython)
  Object1 = Clone063041
  Object2 = Pocket003
  SubElement1 = Face27
  SubElement2 = Face26
  Type = plane
  directionConstraint = 0
  offset = 0
FEATURE [App::FeaturePython] axialConstraint05  label="Arm 4"  # a2plus constraint (typed FeaturePython)
  Object1 = Clone063042
  Object2 = Pocket003
  SubElement1 = Edge24
  SubElement2 = Edge26
  Type = axial
  directionConstraint = 0
  lockRotation = false
FEATURE [App::FeaturePython] planeConstraint27  label="Arm 5"  # a2plus constraint (typed FeaturePython)
  Object1 = Pocket003
  Object2 = Clone063042
  SubElement1 = Face5
  SubElement2 = Face13
  Type = plane
  directionConstraint = 0
  offset = 0
FEATURE [Part::MultiFuse] Fusion004003002002003003  label="Arm assembly001"
  Shapes = -> [Clone063042,Pocket003]
FEATURE [Sketcher::SketchObject] Sketch035  label="Arm-Cylinder geometry003"
  Placement = pos=(0.00708429,2266.89,0.00621209) rot=(1,-2e-06,-2e-06;1.5708rad)
  sketch-geometry (5):
    g0: LineSegment StartX=4541.54 StartY=-31.3638 StartZ=0 EndX=4599.95 EndY=-39.4441 EndZ=0
    g1: LineSegment StartX=4571.34 StartY=-135.302 StartZ=0 EndX=4616.6 EndY=-97.495 EndZ=0
    g2: ArcOfCircle CenterX=4595.43 CenterY=-72.1527 CenterZ=0 NormalX=0 NormalY=0 NormalZ=1 Radius=33.02 StartAngle=5.40828 EndAngle=7.71654
    g3: Circle CenterX=4595.43 CenterY=-72.1527 CenterZ=0 NormalX=0 NormalY=0 NormalZ=1 Radius=13.97
    g4: LineSegment StartX=4541.54 StartY=-31.3638 StartZ=0 EndX=4571.34 EndY=-135.302 EndZ=0
  constraints (12):
    c: Coincident(g0,g2)
    c: Coincident(g1,g2)
    c: Equal(g0,g1)
    c: Tangent(g0,g2)
    c: Tangent(g1,g2)
    c: Radius(g2) = 33.02
    c: Radius(g3) = 13.97
    c: Coincident(g4,g0)
    c: Coincident(g4,g1)
    c: Coincident(g2,g3)
    c: DistanceX(g2) = 4595.43
    c: DistanceY(g2) = -72.1527
FEATURE [Sketcher::SketchObject] Sketch036  label="Arm-Cylinder geometry004"
  Placement = pos=(0.00708429,2273.24,0.00621209) rot=(1,-2e-06,-2e-06;1.5708rad)
  sketch-geometry (8):
    g0: LineSegment [constr] StartX=4637.51 StartY=-735.719 StartZ=0 EndX=4757.5 EndY=-855.7 EndZ=0
    g1: LineSegment StartX=4735.41 StartY=-707.483 StartZ=0 EndX=4808.1 EndY=-813.702 EndZ=0
    g2: ArcOfCircle CenterX=4780.85 CenterY=-832.351 CenterZ=0 NormalX=0 NormalY=0 NormalZ=1 Radius=33.02 StartAngle=3.92703 EndAngle=6.88334
    g3: Circle CenterX=4781.07 CenterY=-832.384 CenterZ=0 NormalX=0 NormalY=0 NormalZ=1 Radius=13.97
    g4: LineSegment StartX=4637.51 StartY=-735.719 StartZ=0 EndX=4735.41 EndY=-707.483 EndZ=0
    g5: LineSegment StartX=4637.51 StartY=-735.719 StartZ=0 EndX=4689.6 EndY=-787.803 EndZ=0
    g6: LineSegment StartX=4757.5 StartY=-855.7 StartZ=0 EndX=4709.36 EndY=-807.559 EndZ=0
    g7: ArcOfCircle CenterX=4699.48 CenterY=-797.681 CenterZ=0 NormalX=0 NormalY=0 NormalZ=1 Radius=13.97 StartAngle=5.49782 EndAngle=8.63942
  constraints (21):
    c: Coincident(g1,g2)
    c: Coincident(g0,g2)
    c: Radius(g2) = 33.02
    c: Tangent(g0,g2)
    c: Tangent(g1,g2)
    c: Radius(g3) = 13.97
    c: Coincident(g4,g0)
    c: Coincident(g4,g1)
    c: Coincident(g5,g0)
    c: PointOnObject(g5,g0)
    c: Coincident(g6,g0)
    c: PointOnObject(g6,g0)
    c: DistanceX(g0) = 4757.5
    c: DistanceY(g0) = -855.7
    c: DistanceX(g0) = 4637.51
    c: DistanceY(g0) = -735.719
    c: PointOnObject(g7,g0)
    c: Coincident(g7,g5)
    c: Coincident(g7,g6)
    c: Distance(g7,g0) = 87.63
    c: Radius(g7) = 13.97
FEATURE [PartDesign::Pad] Pad008003008
  Length = 25.4
  Length2 = 100
  Placement = pos=(0.00708429,2273.24,0.00621209) rot=(1,-2e-06,-2e-06;1.5708rad)
  Reversed = true
  Sketch = -> Sketch036
  Type = 0
FEATURE [Part::MultiFuse] Fusion  label="Loader shaft support"
  Shapes = -> [Clone063026,Clone063027,Clone063028,Clone063029]
FEATURE [Sketcher::SketchObject] Sketch038
  Placement = pos=(0,1515.61,0) rot=(1,0,0;1.5708rad)
  sketch-geometry (1):
    g0: Circle CenterX=-1028.09 CenterY=54.5351 CenterZ=0 NormalX=0 NormalY=0 NormalZ=1 Radius=38.1
  constraints (1):
    c: Radius(g0) = 38.1
FEATURE [PartDesign::Pad] Pad008003010
  Length = 1016
  Length2 = 100
  Placement = pos=(0,1515.61,0) rot=(1,0,0;1.5708rad)
  Reversed = true
  Sketch = -> Sketch038
  Type = 0
FEATURE [Part::Cut] Cut
  Base = -> Fusion
  Tool = -> Pad008003010
FEATURE [App::DocumentObjectGroup] Group001  label="Frame"
  Group = -> [Clone034,Arm_support_01003,Arm_support_01004,Arm_support_01005,Arm_support_01006,Arm_support_01006001,Pocket,Clone063040,Cut]
FEATURE [App::FeaturePython] planeConstraint07  label="planeConstraint07__Cut"  # a2plus constraint (typed FeaturePython)
  Object1 = Arm_support_01
  Object2 = Cut
  SubElement1 = Face16
  SubElement2 = Face44
  Type = plane
  directionConstraint = 1
  offset = 0
FEATURE [App::FeaturePython] planeConstraint07_mirror001  label="planeConstraint07__Arm_support_01"  # a2plus constraint (typed FeaturePython)
  Object1 = Arm_support_01
  Object2 = Cut
  SubElement1 = Face16
  SubElement2 = Face44
  Type = plane
  directionConstraint = 1
  offset = 0
FEATURE [App::FeaturePython] planeConstraint30  # a2plus constraint (typed FeaturePython)
  Object1 = Cut
  Object2 = Pocket
  SubElement1 = Face4
  SubElement2 = Face1
  Type = plane
  directionConstraint = 1
  offset = 0
FEATURE [App::FeaturePython] circularEdgeConstraint01  # a2plus constraint (typed FeaturePython)
  Object1 = Clone063001
  Object2 = Cut
  SubElement1 = Edge3
  SubElement2 = Edge214
  Type = circularEdge
  directionConstraint = 1
  lockRotation = true
  offset = -254
FEATURE [App::FeaturePython] circularEdgeConstraint02  label="circularEdgeConstraint02__Loader cylinder shaft"  # a2plus constraint (typed FeaturePython)
  Object1 = Arm_support_01
  Object2 = Cylinder047
  SubElement1 = Edge93
  SubElement2 = Edge3
  Type = circularEdge
  directionConstraint = 0
  lockRotation = true
  offset = 203.2
FEATURE [App::FeaturePython] circularEdgeConstraint02_mirror  label="circularEdgeConstraint02__Arm_support_01"  # a2plus constraint (typed FeaturePython)
  Object1 = Arm_support_01
  Object2 = Cylinder047
  SubElement1 = Edge93
  SubElement2 = Edge3
  Type = circularEdge
  directionConstraint = 0
  lockRotation = true
  offset = 203.2
FEATURE [App::FeaturePython] circularEdgeConstraint03  # a2plus constraint (typed FeaturePython)
  Object1 = Cylinder047
  Object2 = Clone063034
  SubElement1 = Edge3
  SubElement2 = Edge6
  Type = circularEdge
  directionConstraint = 0
  lockRotation = true
  offset = -12.7
FEATURE [App::FeaturePython] circularEdgeConstraint04  # a2plus constraint (typed FeaturePython)
  Object1 = Cylinder047
  Object2 = Clone063033
  SubElement1 = Edge3
  SubElement2 = Edge12
  Type = circularEdge
  directionConstraint = 0
  lockRotation = true
  offset = -12.7
FEATURE [App::DocumentObjectGroup] Group014  label="Constraints (temporal)"
  Group = -> [planeConstraint30_mirror,axialConstraint04_mirror,circularEdgeConstraint10,circularEdgeConstraint11,planeConstraint04,planeConstraint05,planeConstraint06,axialConstraint05,planeConstraint27,planeConstraint07_mirror001,planeConstraint30,circularEdgeConstraint01,circularEdgeConstraint02_mirror,circularEdgeConstraint03,circularEdgeConstraint04]
FEATURE [Sketcher::SketchObject] Sketch039  label="Arm-Cylinder geometry005"
  Placement = pos=(0.00708429,2266.89,0.00621209) rot=(1,-2e-06,-2e-06;1.5708rad)
  sketch-geometry (6):
    g0: LineSegment StartX=4477.4 StartY=-176.297 StartZ=0 EndX=4420.94 EndY=-192.486 EndZ=0
    g1: LineSegment StartX=4385.74 StartY=-106.068 StartZ=0 EndX=4379.1 EndY=-156.432 EndZ=0
    g2: ArcOfCircle CenterX=4411.84 CenterY=-160.745 CenterZ=0 NormalX=0 NormalY=0 NormalZ=1 Radius=33.02 StartAngle=3.01059 EndAngle=4.99164
    g3: Circle CenterX=4411.84 CenterY=-160.745 CenterZ=0 NormalX=0 NormalY=0 NormalZ=1 Radius=13.97
    g4: LineSegment StartX=4385.74 StartY=-106.068 StartZ=0 EndX=4460.07 EndY=-115.862 EndZ=0
    g5: LineSegment StartX=4460.07 StartY=-115.862 StartZ=0 EndX=4477.4 EndY=-176.297 EndZ=0
  constraints (9):
    c: Coincident(g0,g2)
    c: Coincident(g1,g2)
    c: Tangent(g0,g2)
    c: Tangent(g1,g2)
    c: Radius(g2) = 33.02
    c: Radius(g3) = 13.97
    c: Coincident(g1,g4)
    c: Coincident(g4,g5)
    c: Coincident(g5,g0)
FEATURE [PartDesign::Pad] Pad008003011
  Length = 12.7
  Length2 = 100
  Placement = pos=(0.00708429,2266.89,0.00621209) rot=(1,-2e-06,-2e-06;1.5708rad)
  Sketch = -> Sketch035
  Type = 0
FEATURE [PartDesign::Pad] Pad008003012
  Length = 12.7
  Length2 = 100
  Placement = pos=(0.00708429,2266.89,0.00621209) rot=(1,-2e-06,-2e-06;1.5708rad)
  Reversed = true
  Sketch = -> Sketch039
  Type = 0
FEATURE [Part::FeaturePython] Clone  label="Clone of Pad008003011"  # Draft clone (typed FeaturePython)
  Objects = -> [Pad008003011]
  Placement = pos=(0.00708429,2330.39,0.00621209) rot=(1,-2e-06,-2e-06;1.5708rad)
  Scale = (1,1,1)
FEATURE [Part::FeaturePython] Clone063043  label="Clone of Pad008003012"  # Draft clone (typed FeaturePython)
  Objects = -> [Pad008003012]
  Placement = pos=(0.00708429,2355.79,0.00621209) rot=(1,-2e-06,-2e-06;1.5708rad)
  Scale = (1,1,1)
FEATURE [Part::MultiFuse] Fusion004003002002003004  label="Arm"
  Shapes = -> [Fusion004003002002003003,Pad008003008,Pad008003011,Pad008003012,Clone,Clone063043]
FEATURE [Part::FeaturePython] Clone063044  label="Clone of Arm"  # Draft clone (typed FeaturePython)
  Objects = -> [Fusion004003002002003004]
  Placement = pos=(972.445,-678.528,-1431.21) rot=(0,0,1;0rad)
  Scale = (1,1,1)
FEATURE [Part::FeaturePython] Clone063045  label="Clone of Arm001"  # Draft clone (typed FeaturePython)
  Objects = -> [Fusion004003002002003004]
  Placement = pos=(638.555,-1044.31,-1795.49) rot=(0,0,1;0rad)
  Scale = (1,1,1)
FEATURE [Part::Mirroring] Part__Mirroring  label="Clone of Arm001 (Mirror #1)"
  Base = (0,0,0)
  Normal = (0,1,0)
  Placement = pos=(3770.57,2262.16,1914.12) rot=(0,0,1;0rad)
  Source = -> Clone063045
FEATURE [Part::FeaturePython] Clone063046  label="Clone of Clone of Arm001 (Mirror #1)"  # Draft clone (typed FeaturePython)
  Objects = -> [Part__Mirroring]
  Placement = pos=(333.893,1794.94,364.275) rot=(0,0,1;0rad)
  Scale = (1,1,1)
FEATURE [Part::MultiFuse] Fusion004003002002003005  label="Arms001"
  Shapes = -> [Clone063046,Clone063044]
FEATURE [App::DocumentObjectGroup] Group015  label="Arm (edit here)"
  Group = -> [Clone063041,Sketch032,Fusion004003002002003004,Part__Mirroring,Fusion004003002002003005]
FEATURE [Part::FeaturePython] Clone063047  label="Lowered arms"  # Draft clone (typed FeaturePython)
  Objects = -> [Fusion004003002002003005]
  Placement = pos=(-4574.03,943.253,1286.91) rot=(0,-1,0;0.004014rad)
  Scale = (1,1,1)
FEATURE [Part::FeaturePython] Clone063048  label="Raised arms"  # Draft clone (typed FeaturePython)
  Objects = -> [Fusion004003002002003005]
  Placement = pos=(-2891.14,943.253,-3204.53) rot=(0,-1,0;1.38998rad)
  Scale = (1,1,1)
FEATURE [Part::FeaturePython] Clone063049  label="Clone of Cylinder 36in extended"  # Draft clone (typed FeaturePython)
  Objects = -> [Clone063034]
  Placement = pos=(-557.972,1237.18,-1660.81) rot=(0,-1,0;1.56923rad)
  Scale = (1,1,1)
FEATURE [Part::FeaturePython] Clone063050  label="Clone of Cylinder 36in retracted"  # Draft clone (typed FeaturePython)
  Objects = -> [Clone063033]
  Placement = pos=(-1736.48,1237.18,-239.915) rot=(0,0,1;0rad)
  Scale = (1,1,1)
FEATURE [Part::FeaturePython] Clone063051  label="Clone of 14" cylinder ext"  # Draft clone (typed FeaturePython)
  Objects = -> [Fusion002002001]
  Placement = pos=(146.458,-3389.03,-1155.72) rot=(0.957629,0.161054,0.238764;1.1564rad)
  Scale = (1,1,1)
FEATURE [Part::FeaturePython] Clone063052  label="Clone of 14" cylinder ret"  # Draft clone (typed FeaturePython)
  Objects = -> [Fusion002002002]
  Placement = pos=(-2279.03,1255.8,-2348.22) rot=(0.62855,0.729863,-0.268748;1.8185rad)
  Scale = (1,1,1)
FEATURE [Part::Compound] Compound001010  label="Lowered cylinders"
  Links = -> [Clone063033,Fusion002002002,Clone063050,Clone063052]
FEATURE [Part::Compound] Compound001011  label="Raised cylinders"
  Links = -> [Clone063034,Fusion002002001,Clone063049,Clone063051]
FEATURE [App::DocumentObjectGroup] Group003  label="Arms"
  Group = -> [Clone063001,Group009,Cylinder047,Group015,Compound001,Compound001009,Compound001011,Compound001010,Clone063048,Clone063047]
